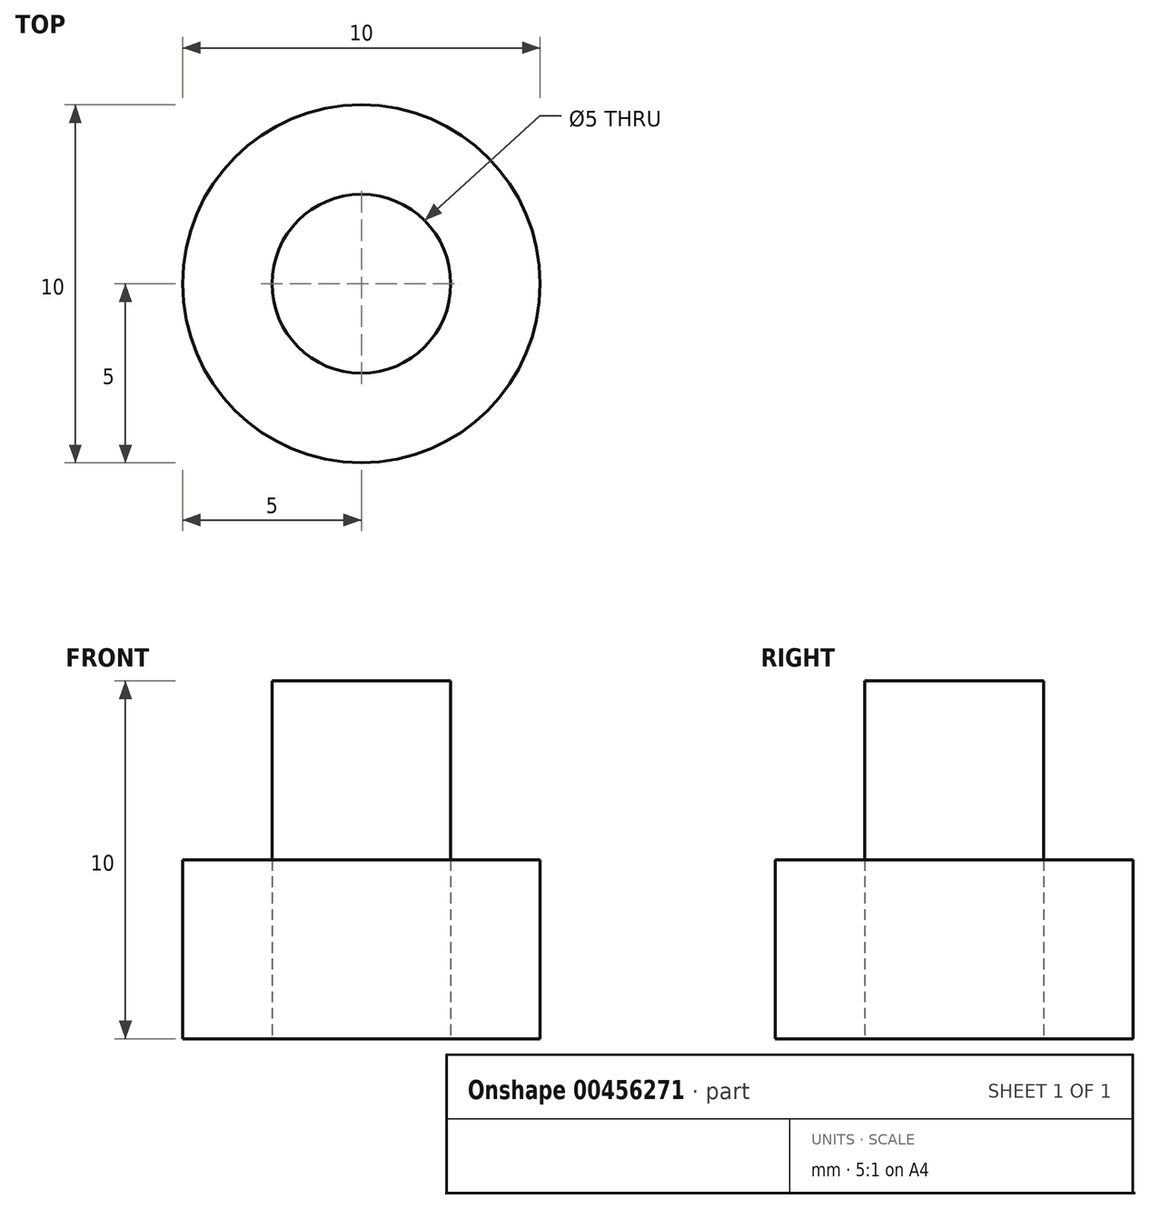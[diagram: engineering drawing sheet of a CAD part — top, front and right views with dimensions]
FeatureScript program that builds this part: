
annotation { "Feature Type Name" : "Feature", "Feature Type Description" : "" }
export const myFeature = defineFeature(function(context is Context, id is Id, definition is map)
    precondition{}
    {
        {
            var Q0;
            Q0=qCreatedBy(makeId("Top.planeOp"),FACE);
            var sketch = newSketch(context, id + "F0", { "sketchPlane" : qUnion([Q0])});
            skCircle(sketch, "E0", {"center": v(0, 0) * mm, "radius": 2.5 * mm});
            skCircle(sketch, "E1", {"center": v(0, 0) * mm, "radius": 5 * mm});
            skSolve(sketch);
        }
        {
            var Q0;
            Q0=makeQuery(id+"F0.imprint","IMPRINT",FACE,{"disambiguationData":[TD([[makeQuery(id+"F0.imprint","IMPRINT",EDGE,{"derivedFrom":sQuery(id+"F0.wireOp",EDGE,"E0")}),1.0]])]});
            extrude(context, id + "F1", {"entities" : qUnion([Q0]), "depth" : 10 * mm, "offsetDistance" : 25 * mm});
        }
        {
            var Q0;
            Q0=makeQuery(id+"F0.imprint","IMPRINT",FACE,{"disambiguationData":[TD([[makeQuery(id+"F0.imprint","IMPRINT",EDGE,{"derivedFrom":sQuery(id+"F0.wireOp",EDGE,"E0")}),-1.0]])]});
            extrude(context, id + "F2", {"entities" : qUnion([Q0]), "depth" : 5 * mm});
        }
    });
